# Revit family: xxxBasin-Wall_Hung-DXV-EQUILITY-D20076001.415
name_source: partatom
category: Plumbing Fixtures
units: mm (PartAtom-declared; Revit-internal decimal feet)

## family parameters
Cut with Voids When Loaded = No
Host = Face
OmniClass Number = 23.45.05.14.14
OmniClass Title = Sinks/Lavatories
Part Type = Normal
Room Calculation Point = No
Round Connector Dimension = Use Diameter
Shared = Yes

## types (1)
- D20076001.415
    ADA Compliant = Yes
    ASME A112.19.2/CSA B45.1 = Yes
    Assembly Code = D2010310
    CW Connection = Yes
    CWFU = 1.5
    Cold Water Connection Height = 19 3/4"
    Cold Water Connection Width = 4"
    Cold Water Diameter = 1/2"
    Default Elevation = 34"
    Description = Equility 33" Wallmount Bathroom Sink
    Drain = Sold Separately
    Finish = Fine Fire Clay-DXV-415-Canvas White
    HW Connection = Yes
    HWFU = 1.5
    Height = 8 9/16"
    Hot Water Connection Height = 19 3/4"
    Hot Water Connection Width = 4"
    Hot Water Diameter = 1/2"
    Installation Instruction Link = https://dxv01.blob.core.windows.net
    Installation Type = Wall Hung
    Length = 17 11/16"
    Manufacturer = DXV
    Material = Fine Fire Clay-DXV-415-Canvas White
    Model = D20076001.415
    Optional Metal Console Legs = No
    Overflow = Hidden
    Product Documentation Link = https://dxv01.blob.core.windows.net
    Product Page URL = https://www.dxv.com
    Revised Date = 11/18/2021
    URL = https://www.dxv.com
    Vent Connection = No
    WFU = 2
    Warranty Documentation Link = https://www.dxv.com
    Waste Connection = Yes
    Waste Connection Diameter = 1 1/4"
    Waste Connection Height = 18 1/8"
    Width = 32 3/4"

## geometry (parser evidence)
native form markers: Sweep x2
no freeform markers — native parametric forms only
